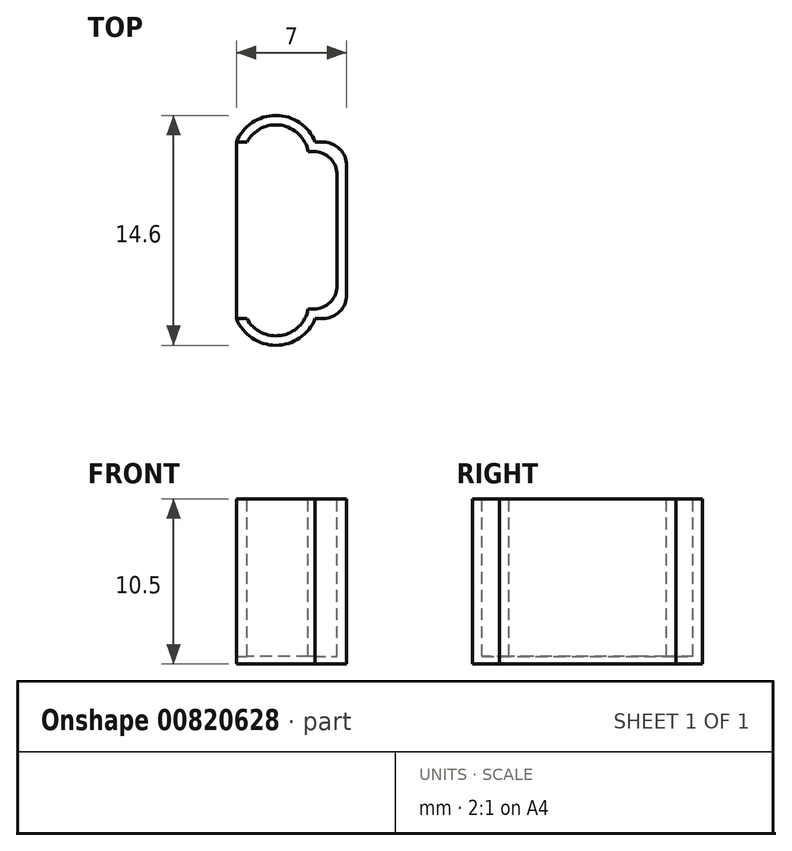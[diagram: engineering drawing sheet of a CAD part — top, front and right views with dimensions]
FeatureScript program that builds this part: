
annotation { "Feature Type Name" : "Feature", "Feature Type Description" : "" }
export const myFeature = defineFeature(function(context is Context, id is Id, definition is map)
    precondition{}
    {
        {
            var Q0;
            Q0=qCreatedBy(makeId("Front.planeOp"),FACE);
            var sketch = newSketch(context, id + "F0", { "sketchPlane" : qUnion([Q0])});
            skLineSegment(sketch, "E0", {"start": v(0, -5.6) * mm, "end": v(0, 5.6) * mm});
            skLineSegment(sketch, "E1", {"start": v(0, 5.6) * mm, "end": v(-2, 5.6) * mm});
            skArc(sketch, "E2", {"start": v(-2, 5.6) * mm, "mid": v(-4.5, 7.3) * mm, "end": v(-7, 5.6) * mm});
            skLineSegment(sketch, "E3", {"start": v(9.25, 0) * mm, "end": v(-12.7, 0) * mm, "construction": true});
            skArc(sketch, "E4.MirrorCS", {"start": v(-2, -5.6) * mm, "mid": v(-4.5, -7.3) * mm, "end": v(-7, -5.6) * mm});
            skLineSegment(sketch, "E5.MirrorCS", {"start": v(0, -5.6) * mm, "end": v(-2, -5.6) * mm});
            skArc(sketch, "E6.0", {"start": v(-2.45, 5) * mm, "mid": v(-4.18, 6.68) * mm, "end": v(-6.34, 5.6) * mm});
            skArc(sketch, "E6.1", {"start": v(-2.45, -5) * mm, "mid": v(-4.18, -6.68) * mm, "end": v(-6.34, -5.6) * mm});
            skLineSegment(sketch, "E6.2", {"start": v(-0.6, -5) * mm, "end": v(-2.45, -5) * mm});
            skLineSegment(sketch, "E6.3", {"start": v(-0.6, -5) * mm, "end": v(-0.6, 5) * mm});
            skLineSegment(sketch, "E6.4", {"start": v(-0.6, 5) * mm, "end": v(-2.45, 5) * mm});
            skLineSegment(sketch, "E7", {"start": v(-7, 5.6) * mm, "end": v(-6.34, 5.6) * mm});
            skLineSegment(sketch, "E8", {"start": v(-6.34, -5.6) * mm, "end": v(-7, -5.6) * mm});
            skSolve(sketch);
        }
        {
            var Q0;
            Q0=makeQuery(id+"F0.imprint","IMPRINT",FACE,{"disambiguationData":[TD([[makeQuery(id+"F0.imprint","IMPRINT",EDGE,{"derivedFrom":sQuery(id+"F0.wireOp",EDGE,"E0")}),1.0]])]});
            extrude(context, id + "F1", {"entities" : qUnion([Q0]), "depth" : 10 * mm, "offsetDistance" : 25 * mm});
        }
        {
            var Q0;
            Q0=makeQuery(id+"F1.opExtrude","SWEPT_EDGE",EDGE,{"disambiguationData":[OSD([sQuery(id+"F0.wireOp",EDGE,"E0"),sQuery(id+"F0.wireOp",EDGE,"E1")])]});
            var Q1;
            Q1=makeQuery(id+"F1.opExtrude","SWEPT_EDGE",EDGE,{"disambiguationData":[OSD([sQuery(id+"F0.wireOp",EDGE,"E0"),sQuery(id+"F0.wireOp",EDGE,"E5.MirrorCS")])]});
            var Q2;
            Q2=makeQuery(id+"F1.opExtrude","SWEPT_EDGE",EDGE,{"disambiguationData":[OSD([sQuery(id+"F0.wireOp",EDGE,"E6.3"),sQuery(id+"F0.wireOp",EDGE,"E6.4")])]});
            var Q3;
            Q3=makeQuery(id+"F1.opExtrude","SWEPT_EDGE",EDGE,{"disambiguationData":[OSD([sQuery(id+"F0.wireOp",EDGE,"E6.2"),sQuery(id+"F0.wireOp",EDGE,"E6.3")])]});
            fillet(context, id + "F2", {"entities" : qUnion([Q0, Q1, Q2, Q3]), "radius" : 1.5 * mm, "tangentPropagation" : true, "allowEdgeOverflow" : false});
        }
        {
            var Q0;
            Q0=makeQuery(id+"F1.opExtrude","CAP_FACE",FACE,{"disambiguationData":[OSD([sQuery(id+"F0.wireOp",EDGE,"E0"),sQuery(id+"F0.wireOp",EDGE,"E1"),sQuery(id+"F0.wireOp",EDGE,"E2"),sQuery(id+"F0.wireOp",EDGE,"E4.MirrorCS"),sQuery(id+"F0.wireOp",EDGE,"E5.MirrorCS"),sQuery(id+"F0.wireOp",EDGE,"E6.0"),sQuery(id+"F0.wireOp",EDGE,"E6.1"),sQuery(id+"F0.wireOp",EDGE,"E6.2"),sQuery(id+"F0.wireOp",EDGE,"E6.3"),sQuery(id+"F0.wireOp",EDGE,"E6.4"),sQuery(id+"F0.wireOp",EDGE,"E7"),sQuery(id+"F0.wireOp",EDGE,"E8")])],"isStart":false});
            var sketch = newSketch(context, id + "F3", { "sketchPlane" : qUnion([Q0])});
            skArc(sketch, "E9.0", {"start": v(-2, 5.6) * mm, "mid": v(-4.5, 7.3) * mm, "end": v(-7, 5.6) * mm});
            skLineSegment(sketch, "E10.0.0", {"start": v(-2, -5.6) * mm, "end": v(-1.5, -5.6) * mm});
            skArc(sketch, "E10.0.1", {"start": v(-1.5, -5.6) * mm, "mid": v(-0.44, -5.16) * mm, "end": v(0, -4.1) * mm});
            skLineSegment(sketch, "E10.0.2", {"start": v(0, -4.1) * mm, "end": v(0, 4.1) * mm});
            skArc(sketch, "E10.0.3", {"start": v(0, 4.1) * mm, "mid": v(-0.44, 5.16) * mm, "end": v(-1.5, 5.6) * mm});
            skLineSegment(sketch, "E10.0.4", {"start": v(-1.5, 5.6) * mm, "end": v(-2, 5.6) * mm});
            skLineSegment(sketch, "E10.0.14", {"start": v(-6.34, -5.6) * mm, "end": v(-7, -5.6) * mm});
            skArc(sketch, "E10.0.15", {"start": v(-7, -5.6) * mm, "mid": v(-4.5, -7.3) * mm, "end": v(-2, -5.6) * mm});
            skLineSegment(sketch, "E11", {"start": v(-7, 5.6) * mm, "end": v(-7, -5.6) * mm});
            skPoint(sketch, "E10.0.6.end.orphan", {"position": v(-6.34, 5.6) * mm});
            skPoint(sketch, "E10.0.8.start.orphan", {"position": v(-2.45, 5) * mm});
            skPoint(sketch, "E10.0.9.start.orphan", {"position": v(-2.1, 5) * mm});
            skPoint(sketch, "E10.0.10.start.orphan", {"position": v(-0.6, 3.5) * mm});
            skPoint(sketch, "E10.0.11.start.orphan", {"position": v(-0.6, -3.5) * mm});
            skPoint(sketch, "E10.0.12.end.orphan", {"position": v(-2.45, -5) * mm});
            skPoint(sketch, "E10.0.12.start.orphan", {"position": v(-2.1, -5) * mm});
            skSolve(sketch);
        }
        {
            var Q0;
            Q0=makeQuery(id+"F3.imprint","IMPRINT",FACE,{"disambiguationData":[TD([[makeQuery(id+"F3.imprint","IMPRINT",EDGE,{"derivedFrom":sQuery(id+"F3.wireOp",EDGE,"E10.0.14")}),-1.0]])]});
            var Q1;
            Q1=makeQuery(id+"F3.imprint","IMPRINT",FACE,{"disambiguationData":[TD([[makeQuery(id+"F3.imprint","IMPRINT",EDGE,{"derivedFrom":sQuery(id+"F3.wireOp",EDGE,"E10.0.0")}),-1.0]])]});
            extrude(context, id + "F4", {"entities" : qUnion([Q0, Q1]), "operationType" : NewBodyOperationType.ADD, "depth" : 0.5 * mm, "offsetDistance" : 25 * mm});
        }
        {
            var Q0;
            Q0=makeQuery(id+"F1.opExtrude","SWEPT_BODY",BODY,{"disambiguationData":[OSD([sQuery(id+"F0.wireOp",EDGE,"E0"),sQuery(id+"F0.wireOp",EDGE,"E1"),sQuery(id+"F0.wireOp",EDGE,"E2"),sQuery(id+"F0.wireOp",EDGE,"E4.MirrorCS"),sQuery(id+"F0.wireOp",EDGE,"E5.MirrorCS"),sQuery(id+"F0.wireOp",EDGE,"E6.0"),sQuery(id+"F0.wireOp",EDGE,"E6.1"),sQuery(id+"F0.wireOp",EDGE,"E6.2"),sQuery(id+"F0.wireOp",EDGE,"E6.3"),sQuery(id+"F0.wireOp",EDGE,"E6.4"),sQuery(id+"F0.wireOp",EDGE,"E7"),sQuery(id+"F0.wireOp",EDGE,"E8")])]});
            var Q1;
            Q1=makeQuery(id+"F4.opExtrude","CAP_EDGE",EDGE,{"disambiguationData":[OSD([sQuery(id+"F3.wireOp",EDGE,"E10.0.4")])],"isStart":false});
            transform(context, id + "F5", {"entities" : qUnion([Q0]), "transformType" : TransformType.ROTATION, "transformAxis" : qUnion([Q1]), "angle" : 90 * degree, "oppositeDirection" : true, "makeCopy" : false});
        }
    });
